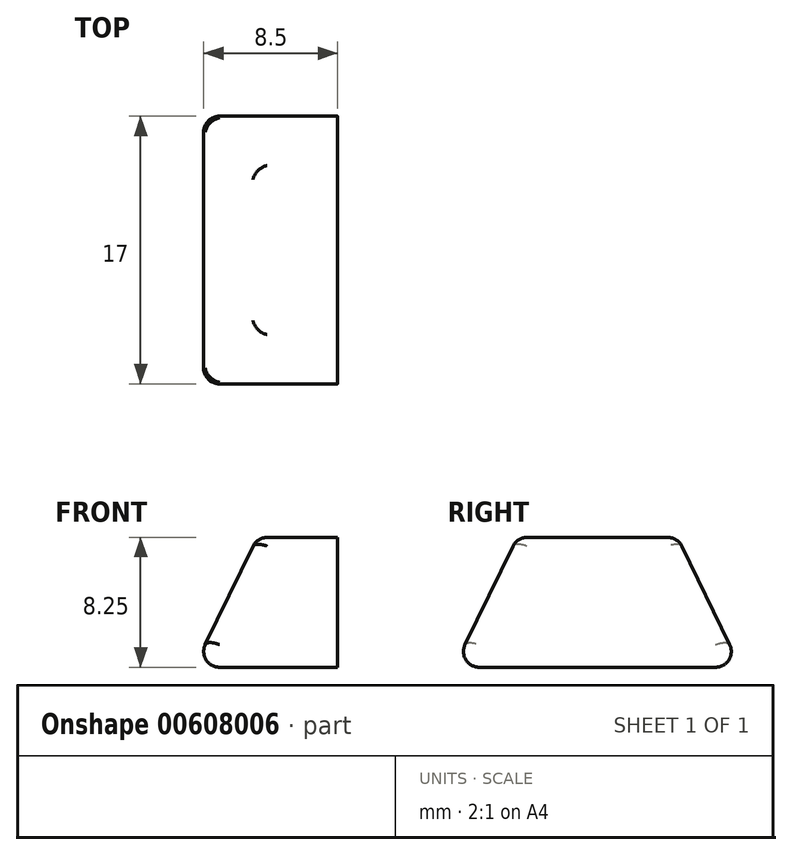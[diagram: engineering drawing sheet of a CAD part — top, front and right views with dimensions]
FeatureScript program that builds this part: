
annotation { "Feature Type Name" : "Feature", "Feature Type Description" : "" }
export const myFeature = defineFeature(function(context is Context, id is Id, definition is map)
    precondition{}
    {
        {
            var Q0;
            Q0=qCreatedBy(makeId("Top.planeOp"),FACE);
            var sketch = newSketch(context, id + "F0", { "sketchPlane" : qUnion([Q0])});
            skLineSegment(sketch, "E0.bottom", {"start": v(0, -9.1) * mm, "end": v(-9.1, -9.1) * mm});
            skLineSegment(sketch, "E0.top", {"start": v(0, 9.1) * mm, "end": v(-9.1, 9.1) * mm});
            skLineSegment(sketch, "E0.right", {"start": v(-9.1, -9.1) * mm, "end": v(-9.1, 9.1) * mm});
            skPoint(sketch, "E0.middle", {"position": v(0, 0) * mm});
            skLineSegment(sketch, "E1.bottom", {"start": v(0, -5.1) * mm, "end": v(-5.1, -5.1) * mm});
            skLineSegment(sketch, "E1.top", {"start": v(0, 5.1) * mm, "end": v(-5.1, 5.1) * mm});
            skLineSegment(sketch, "E1.right", {"start": v(-5.1, -5.1) * mm, "end": v(-5.1, 5.1) * mm});
            skPoint(sketch, "E2.endSnap0", {"position": v(0, -9.1) * mm});
            skLineSegment(sketch, "E3", {"start": v(0, 9.1) * mm, "end": v(0, -9.1) * mm});
            skSolve(sketch);
        }
        {
            var Q0;
            {var subQ2=sQuery(id+"F0.wireOp",EDGE,"E0.bottom");Q0=makeQuery(id+"F0.imprint","IMPRINT",FACE,{"disambiguationData":[TD([[makeQuery(id+"F0.imprint","IMPRINT",EDGE,{"derivedFrom":subQ2}),-1.0]])]});}
            var Q1;
            {var subQ0=sQuery(id+"F0.wireOp",EDGE,"E1.bottom");Q1=makeQuery(id+"F0.imprint","IMPRINT",FACE,{"disambiguationData":[TD([[makeQuery(id+"F0.imprint","IMPRINT",EDGE,{"derivedFrom":subQ0}),-1.0]])]});}
            extrude(context, id + "F1", {"entities" : qUnion([Q0, Q1]), "depth" : 8.25 * mm, "offsetDistance" : 25 * mm});
        }
        {
            var Q0;
            Q0=makeQuery(id+"F1.opExtrude","CAP_EDGE",EDGE,{"disambiguationData":[OSD([sQuery(id+"F0.wireOp",EDGE,"E0.right")])],"isStart":false});
            var Q1;
            Q1=makeQuery(id+"F1.opExtrude","CAP_EDGE",EDGE,{"disambiguationData":[OSD([sQuery(id+"F0.wireOp",EDGE,"E0.bottom")])],"isStart":false});
            var Q2;
            Q2=makeQuery(id+"F1.opExtrude","CAP_EDGE",EDGE,{"disambiguationData":[OSD([sQuery(id+"F0.wireOp",EDGE,"E0.top")])],"isStart":false});
            chamfer(context, id + "F2", {"entities" : qUnion([Q0, Q1, Q2]), "chamferType" : ChamferType.TWO_OFFSETS, "width1" : 8.25 * mm, "oppositeDirection" : false, "width2" : 4 * mm, "tangentPropagation" : true});
        }
        {
            var Q0;
            Q0=makeQuery(id+"F2.opChamfer","BLEND_EDGE",EDGE,{"blendedFrom":[makeQuery(id+"F1.opExtrude","CAP_EDGE",EDGE,{"disambiguationData":[OSD([sQuery(id+"F0.wireOp",EDGE,"E0.top")])],"isStart":false}),makeQuery(id+"F1.opExtrude","CAP_EDGE",EDGE,{"disambiguationData":[OSD([sQuery(id+"F0.wireOp",EDGE,"E0.right")])],"isStart":false})],"blendedInto":[]});
            var Q1;
            Q1=makeQuery(id+"F2.opChamfer","BLEND_EDGE",EDGE,{"blendedFrom":[makeQuery(id+"F1.opExtrude","CAP_EDGE",EDGE,{"disambiguationData":[OSD([sQuery(id+"F0.wireOp",EDGE,"E0.bottom")])],"isStart":false}),makeQuery(id+"F1.opExtrude","CAP_EDGE",EDGE,{"disambiguationData":[OSD([sQuery(id+"F0.wireOp",EDGE,"E0.right")])],"isStart":false})],"blendedInto":[]});
            var Q2;
            {var subQ0=sQuery(id+"F0.wireOp",EDGE,"E0.bottom");Q2=makeQuery(id+"F2.opChamfer","BLEND_EDGE",EDGE,{"blendedFrom":[makeQuery(id+"F1.opExtrude","CAP_EDGE",EDGE,{"disambiguationData":[OSD([subQ0])],"isStart":false}),makeQuery(id+"F1.opExtrude","CAP_FACE",FACE,{"disambiguationData":[OSD([subQ0,sQuery(id+"F0.wireOp",EDGE,"E0.top"),sQuery(id+"F0.wireOp",EDGE,"E0.right"),sQuery(id+"F0.wireOp",EDGE,"E3")])],"isStart":false})],"blendedInto":[makeQuery(id+"F1.opExtrude","CAP_FACE",FACE,{"disambiguationData":[OSD([subQ0,sQuery(id+"F0.wireOp",EDGE,"E0.top"),sQuery(id+"F0.wireOp",EDGE,"E0.right"),sQuery(id+"F0.wireOp",EDGE,"E3")])],"isStart":false})]});}
            var Q3;
            {var subQ0=sQuery(id+"F0.wireOp",EDGE,"E0.right");Q3=makeQuery(id+"F2.opChamfer","BLEND_EDGE",EDGE,{"blendedFrom":[makeQuery(id+"F1.opExtrude","CAP_EDGE",EDGE,{"disambiguationData":[OSD([subQ0])],"isStart":false}),makeQuery(id+"F1.opExtrude","CAP_FACE",FACE,{"disambiguationData":[OSD([sQuery(id+"F0.wireOp",EDGE,"E0.bottom"),sQuery(id+"F0.wireOp",EDGE,"E0.top"),subQ0,sQuery(id+"F0.wireOp",EDGE,"E3")])],"isStart":false})],"blendedInto":[makeQuery(id+"F1.opExtrude","CAP_FACE",FACE,{"disambiguationData":[OSD([sQuery(id+"F0.wireOp",EDGE,"E0.bottom"),sQuery(id+"F0.wireOp",EDGE,"E0.top"),subQ0,sQuery(id+"F0.wireOp",EDGE,"E3")])],"isStart":false})]});}
            var Q4;
            {var subQ0=sQuery(id+"F0.wireOp",EDGE,"E0.top");Q4=makeQuery(id+"F2.opChamfer","BLEND_EDGE",EDGE,{"blendedFrom":[makeQuery(id+"F1.opExtrude","CAP_EDGE",EDGE,{"disambiguationData":[OSD([subQ0])],"isStart":false}),makeQuery(id+"F1.opExtrude","CAP_FACE",FACE,{"disambiguationData":[OSD([sQuery(id+"F0.wireOp",EDGE,"E0.bottom"),subQ0,sQuery(id+"F0.wireOp",EDGE,"E0.right"),sQuery(id+"F0.wireOp",EDGE,"E3")])],"isStart":false})],"blendedInto":[makeQuery(id+"F1.opExtrude","CAP_FACE",FACE,{"disambiguationData":[OSD([sQuery(id+"F0.wireOp",EDGE,"E0.bottom"),subQ0,sQuery(id+"F0.wireOp",EDGE,"E0.right"),sQuery(id+"F0.wireOp",EDGE,"E3")])],"isStart":false})]});}
            var Q5;
            Q5=makeQuery(id+"F2.opChamfer","BLEND_FACE",FACE,{"disambiguationData":[OSD([sQuery(id+"F0.wireOp",EDGE,"E0.right")])]});
            var Q6;
            {var subQ0=sQuery(id+"F0.wireOp",EDGE,"E0.bottom");Q6=makeQuery(id+"F2.opChamfer","BLEND_EDGE",EDGE,{"blendedFrom":[makeQuery(id+"F1.opExtrude","CAP_EDGE",EDGE,{"disambiguationData":[OSD([subQ0])],"isStart":false}),makeQuery(id+"F1.opExtrude","CAP_FACE",FACE,{"disambiguationData":[OSD([subQ0,sQuery(id+"F0.wireOp",EDGE,"E0.top"),sQuery(id+"F0.wireOp",EDGE,"E0.right"),sQuery(id+"F0.wireOp",EDGE,"E3")])],"isStart":true})],"blendedInto":[makeQuery(id+"F1.opExtrude","CAP_FACE",FACE,{"disambiguationData":[OSD([subQ0,sQuery(id+"F0.wireOp",EDGE,"E0.top"),sQuery(id+"F0.wireOp",EDGE,"E0.right"),sQuery(id+"F0.wireOp",EDGE,"E3")])],"isStart":true})]});}
            var Q7;
            {var subQ0=sQuery(id+"F0.wireOp",EDGE,"E0.top");Q7=makeQuery(id+"F2.opChamfer","BLEND_EDGE",EDGE,{"blendedFrom":[makeQuery(id+"F1.opExtrude","CAP_EDGE",EDGE,{"disambiguationData":[OSD([subQ0])],"isStart":false}),makeQuery(id+"F1.opExtrude","CAP_FACE",FACE,{"disambiguationData":[OSD([sQuery(id+"F0.wireOp",EDGE,"E0.bottom"),subQ0,sQuery(id+"F0.wireOp",EDGE,"E0.right"),sQuery(id+"F0.wireOp",EDGE,"E3")])],"isStart":true})],"blendedInto":[makeQuery(id+"F1.opExtrude","CAP_FACE",FACE,{"disambiguationData":[OSD([sQuery(id+"F0.wireOp",EDGE,"E0.bottom"),subQ0,sQuery(id+"F0.wireOp",EDGE,"E0.right"),sQuery(id+"F0.wireOp",EDGE,"E3")])],"isStart":true})]});}
            fillet(context, id + "F3", {"entities" : qUnion([Q0, Q1, Q2, Q3, Q4, Q5, Q6, Q7]), "radius" : 1 * mm, "tangentPropagation" : true, "allowEdgeOverflow" : false});
        }
    });
